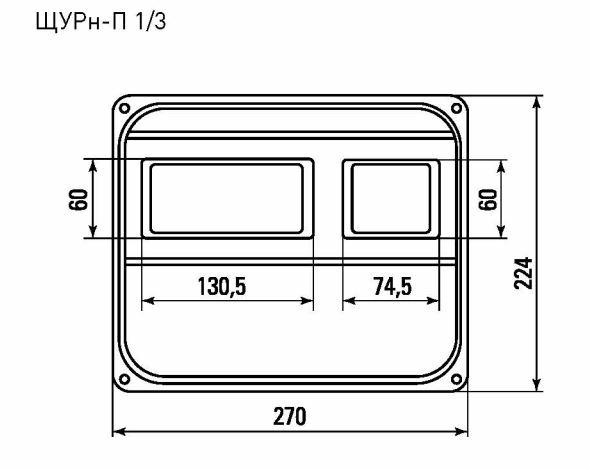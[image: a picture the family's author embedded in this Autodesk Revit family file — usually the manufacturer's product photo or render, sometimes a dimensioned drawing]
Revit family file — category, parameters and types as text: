
# Revit family: EKF_EE_Щит_Этажный_Усиленный_IP31_Basic
name_source: partatom
category: Электрооборудование
units: mm (PartAtom-declared; Revit-internal decimal feet)

## family parameters
Всегда вертикально = Да
На основе рабочей плоскости = Нет
Общий = Нет
При загрузке вырезать с полостями = Нет
Размер круглого соединителя = Использовать диаметр
Тип детали = Силовой щит
Точка расчета площади = Да

## types (6) — shared parameters
ADSK_Единица измерения = компл.
ADSK_Завод-изготовитель = EKF
ADSK_Количество = 1
ADSK_Материал = RAL 7035_Сталь
ADSK_Размер_Высота = 1000 мм
ADSK_Размер_Глубина = 157 мм
ADSK_Размер_Ширина = 960 мм
Изготовитель = EKF
Серия номенклатуры = Basic
Степень защиты IP = IP31
ТВ = EKF
Тип установки = Встраиваемый
zero-valued in all types: ADSK_Масса, Количество модулей на DIN-рейке, Максимальное количество модулей

## per-type parameters (varying)
| type | ADSK_Код изделия | ADSK_Марка | ADSK_Наименование | ADSK_Обозначение | Количество DIN-реек | Описание | Тип |
| ЩЭ 2 кв. усиленный (1000х960х157) IP31 EKF Basic | mb02-v-2-bas | ЩЭ 2 квартиры усиленный IP31 | Щит этажный 2 квартиры усиленный (1000х960х157) IP31 EKF Basic | ЩЭ 2 квартиры усиленный IP31 | 2 | Щит этажный 2 квартиры усиленный (1000х960х157) IP31 EKF Basic | 196 мм |
| ЩЭ 3 кв. усиленный (1000х960х157) IP31 EKF Basic | mb02-v-3-bas | ЩЭ 3 квартир усиленный IP31 | Щит этажный 3 квартир усиленный (1000х960х157) IP31 EKF Basic | ЩЭ 3 квартир усиленный IP31 | 4 | Щит этажный 3 квартир усиленный (1000х960х157) IP31 EKF Basic | 197 мм |
| ЩЭ 4 кв. усиленный (1000х960х157) IP31 EKF Basic | mb02-v-4-bas | ЩЭ 4 квартиры усиленный IP31 | Щит этажный 4 квартиры усиленный (1000х960х157) IP31 EKF Basic | ЩЭ 4 квартиры усиленный IP31 | 4 | Щит этажный 4 квартиры усиленный (1000х960х157) IP31 EKF Basic | 198 мм |
| ЩЭ 4 кв. усиленный без окон (1000х960х157) IP31 EKF Basic | mb02-v-4s-bas | ЩЭ 4 квартиры усиленный без окон IP31 | Щит этажный 4 квартиры усиленный без окон (1000х960х157) IP31 EKF Basic | ЩЭ 4 квартиры усиленный без окон IP31 | 4 | Щит этажный 4 квартиры усиленный без окон (1000х960х157) IP31 EKF Basic | 199 мм |
| ЩЭ 5 кв. усиленный (1000х960х157) IP31 EKF Basic | mb02-v-5-bas | ЩЭ 5 квартир усиленный IP31 | Щит этажный 5 квартир усиленный (1000х960х157) IP31 EKF Basic | ЩЭ 5 квартир усиленный IP31 | 4 | Щит этажный 5 квартир усиленный (1000х960х157) IP31 EKF Basic | 200 мм |
| ЩЭ 6 кв. усиленный (1000х960х157) IP31 EKF Basic | mb02-v-6-bas | ЩЭ 6 квартир усиленный IP31 | Щит этажный 6 квартир усиленный (1000х960х157) IP31 EKF Basic | ЩЭ 6 квартир усиленный IP31 | 4 | Щит этажный 6 квартир усиленный (1000х960х157) IP31 EKF Basic | 201 мм |
